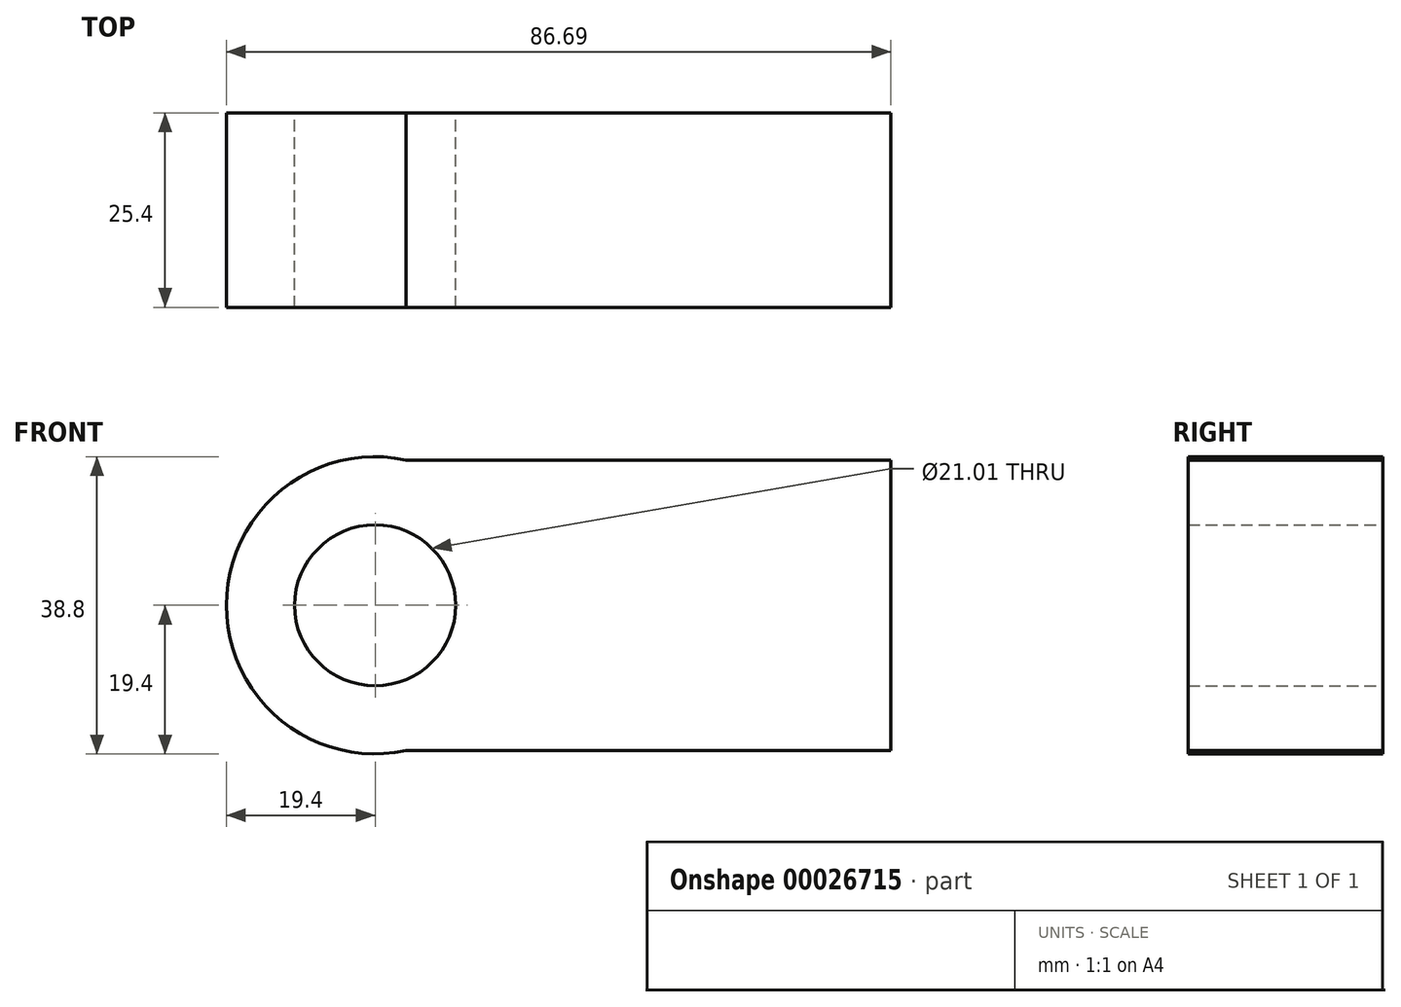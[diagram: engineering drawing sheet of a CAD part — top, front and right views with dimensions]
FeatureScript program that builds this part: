
annotation { "Feature Type Name" : "Feature", "Feature Type Description" : "" }
export const myFeature = defineFeature(function(context is Context, id is Id, definition is map)
    precondition{}
    {
        {
            var Q0;
            Q0=qCreatedBy(makeId("Front.planeOp"),FACE);
            var sketch = newSketch(context, id + "F0", { "sketchPlane" : qUnion([Q0])});
            skLineSegment(sketch, "E0.bottom", {"start": v(-67.29, 18.98) * mm, "end": v(0, 18.98) * mm});
            skLineSegment(sketch, "E0.top", {"start": v(-67.29, -18.98) * mm, "end": v(0, -18.98) * mm});
            skLineSegment(sketch, "E0.right", {"start": v(40.11, 18.98) * mm, "end": v(40.11, 18.8) * mm});
            skArc(sketch, "E1", {"start": v(-63.24, 18.98) * mm, "mid": v(-86.7, 0) * mm, "end": v(-63.24, -18.98) * mm});
            skLineSegment(sketch, "E2.trimOffspring", {"start": v(40.11, -18.8) * mm, "end": v(40.11, -18.98) * mm});
            skCircle(sketch, "E3", {"center": v(-67.29, 0) * mm, "radius": 10.5 * mm});
            skLineSegment(sketch, "E4", {"start": v(0, 18.98) * mm, "end": v(0, -18.98) * mm});
            skPoint(sketch, "E5.center.orphan", {"position": v(40.11, 0) * mm});
            skSolve(sketch);
        }
        {
            var Q0;
            {var subQ1=sQuery(id+"F0.wireOp",EDGE,"E1");Q0=makeQuery(id+"F0.imprint","IMPRINT",FACE,{"disambiguationData":[TD([[makeQuery(id+"F0.imprint","IMPRINT",EDGE,{"derivedFrom":subQ1}),1.0]])]});}
            extrude(context, id + "F1", {"entities" : qUnion([Q0]), "depth" : 25.4 * mm});
        }
    });
